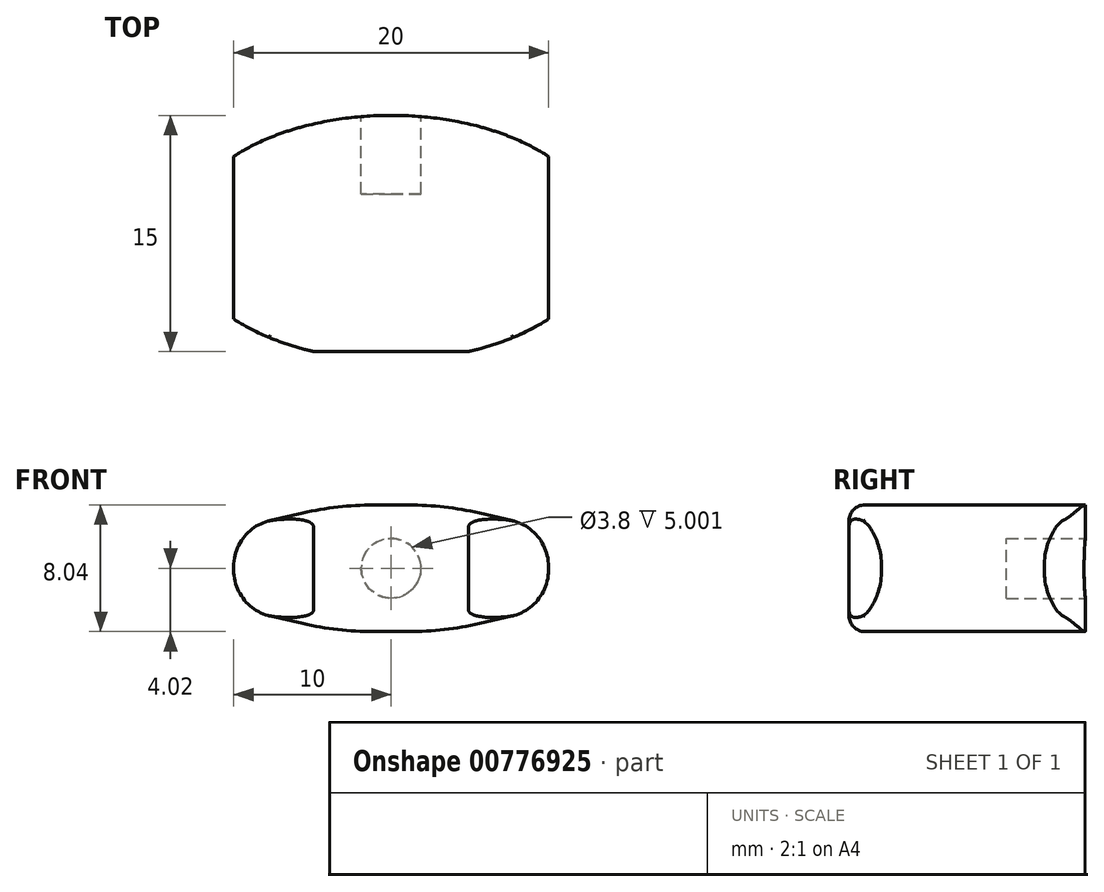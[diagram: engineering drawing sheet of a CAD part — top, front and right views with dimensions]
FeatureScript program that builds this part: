
annotation { "Feature Type Name" : "Feature", "Feature Type Description" : "" }
export const myFeature = defineFeature(function(context is Context, id is Id, definition is map)
    precondition{}
    {
        {
            var Q0;
            Q0=qCreatedBy(makeId("Front.planeOp"),FACE);
            var sketch = newSketch(context, id + "F0", { "sketchPlane" : qUnion([Q0])});
            skLineSegment(sketch, "E0.bottom", {"start": v(3.4, -4.02) * mm, "end": v(-3.4, -4.02) * mm});
            skLineSegment(sketch, "E0.top", {"start": v(3.4, 4.02) * mm, "end": v(-3.4, 4.02) * mm});
            skLineSegment(sketch, "E0.left", {"start": v(10, -2.5) * mm, "end": v(10, 2.5) * mm});
            skLineSegment(sketch, "E0.right", {"start": v(-10, -2.5) * mm, "end": v(-10, 2.5) * mm});
            skPoint(sketch, "E0.middle", {"position": v(0, 0) * mm});
            skLineSegment(sketch, "E1", {"start": v(10, -2.5) * mm, "end": v(3.4, -4.02) * mm});
            skPoint(sketch, "E2.orphan", {"position": v(10, -4.02) * mm});
            skLineSegment(sketch, "E3.MirrorCS", {"start": v(10, 2.5) * mm, "end": v(3.4, 4.02) * mm});
            skLineSegment(sketch, "E4.MirrorCS", {"start": v(-10, -2.5) * mm, "end": v(-3.4, -4.02) * mm});
            skLineSegment(sketch, "E5.MirrorCS", {"start": v(-10, 2.5) * mm, "end": v(-3.4, 4.02) * mm});
            skPoint(sketch, "E6.orphan", {"position": v(10, 4.02) * mm});
            skPoint(sketch, "E7.orphan", {"position": v(-10, 4.02) * mm});
            skPoint(sketch, "E8.orphan", {"position": v(-10, -4.02) * mm});
            skSolve(sketch);
        }
        {
            var Q0;
            Q0 = qSketchRegion(id + "F0", true);
            extrude(context, id + "F1", {"entities" : qUnion([Q0]), "depth" : 15 * mm, "offsetDistance" : 25 * mm});
        }
        {
            var Q0;
            Q0=qCreatedBy(makeId("Front.planeOp"),FACE);
            var sketch = newSketch(context, id + "F2", { "sketchPlane" : qUnion([Q0])});
            skCircle(sketch, "E9", {"center": v(0, 0) * mm, "radius": 1.9 * mm});
            skSolve(sketch);
        }
        {
            var Q0;
            Q0 = qSketchRegion(id + "F2", true);
            extrude(context, id + "F3", {"entities" : qUnion([Q0]), "operationType" : NewBodyOperationType.REMOVE, "depth" : 5 * mm, "offsetDistance" : 25 * mm});
        }
        {
            var Q0;
            Q0=qCreatedBy(makeId("Top.planeOp"),FACE);
            var sketch = newSketch(context, id + "F4", { "sketchPlane" : qUnion([Q0])});
            skEllipse(sketch, "E10", {"center": v(0, -7.77) * mm, "majorRadius": 7.77 * mm, "minorRadius": 13.38 * mm, "majorAxis": v(0, 1)});
            skSolve(sketch);
        }
        {
            var Q0;
            Q0 = qSketchRegion(id + "F4", true);
            extrude(context, id + "F5", {"entities" : qUnion([Q0]), "operationType" : NewBodyOperationType.INTERSECT, "oppositeDirection" : true, "depth" : 25 * mm, "offsetDistance" : 25 * mm, "hasSecondDirection" : true, "secondDirectionOppositeDirection" : false, "secondDirectionDepth" : 25 * mm});
        }
        {
            var Q0;
            Q0=makeQuery(id+"F1.opExtrude","SWEPT_EDGE",EDGE,{"disambiguationData":[OSD([sQuery(id+"F0.wireOp",EDGE,"E0.bottom"),sQuery(id+"F0.wireOp",EDGE,"E1")])]});
            var Q1;
            Q1=makeQuery(id+"F1.opExtrude","SWEPT_EDGE",EDGE,{"disambiguationData":[OSD([sQuery(id+"F0.wireOp",EDGE,"E0.bottom"),sQuery(id+"F0.wireOp",EDGE,"E4.MirrorCS")])]});
            var Q2;
            Q2=makeQuery(id+"F1.opExtrude","SWEPT_EDGE",EDGE,{"disambiguationData":[OSD([sQuery(id+"F0.wireOp",EDGE,"E0.top"),sQuery(id+"F0.wireOp",EDGE,"E3.MirrorCS")])]});
            var Q3;
            Q3=makeQuery(id+"F1.opExtrude","SWEPT_EDGE",EDGE,{"disambiguationData":[OSD([sQuery(id+"F0.wireOp",EDGE,"E0.top"),sQuery(id+"F0.wireOp",EDGE,"E5.MirrorCS")])]});
            fillet(context, id + "F6", {"entities" : qUnion([Q0, Q1, Q2, Q3]), "radius" : 20 * mm, "tangentPropagation" : true, "allowEdgeOverflow" : false});
        }
        {
            var Q0;
            Q0=makeQuery(id+"F1.opExtrude","SWEPT_EDGE",EDGE,{"disambiguationData":[OSD([sQuery(id+"F0.wireOp",EDGE,"E0.right"),sQuery(id+"F0.wireOp",EDGE,"E4.MirrorCS")])]});
            var Q1;
            Q1=makeQuery(id+"F1.opExtrude","SWEPT_EDGE",EDGE,{"disambiguationData":[OSD([sQuery(id+"F0.wireOp",EDGE,"E0.right"),sQuery(id+"F0.wireOp",EDGE,"E5.MirrorCS")])]});
            var Q2;
            Q2=makeQuery(id+"F1.opExtrude","SWEPT_EDGE",EDGE,{"disambiguationData":[OSD([sQuery(id+"F0.wireOp",EDGE,"E0.left"),sQuery(id+"F0.wireOp",EDGE,"E1")])]});
            var Q3;
            Q3=makeQuery(id+"F1.opExtrude","SWEPT_EDGE",EDGE,{"disambiguationData":[OSD([sQuery(id+"F0.wireOp",EDGE,"E0.left"),sQuery(id+"F0.wireOp",EDGE,"E3.MirrorCS")])]});
            fillet(context, id + "F7", {"entities" : qUnion([Q0, Q1, Q2, Q3]), "radius" : 3 * mm, "tangentPropagation" : true, "allowEdgeOverflow" : false});
        }
        {
            var Q0;
            {var subQ0=sQuery(id+"F0.wireOp",EDGE,"E0.top");var subQ1=sQuery(id+"F0.wireOp",EDGE,"E3.MirrorCS");Q0=makeQuery(id+"F6.opFillet","BLEND_EDGE",EDGE,{"blendedFrom":[makeQuery(id+"F1.opExtrude","SWEPT_EDGE",EDGE,{"disambiguationData":[OSD([subQ0,subQ1])]}),makeQuery(id+"F5.boolean.opBoolean","COPY",FACE,{"disambiguationData":[TD([makeQuery(id+"F1.opExtrude","SWEPT_FACE",FACE,{"disambiguationData":[OSD([sQuery(id+"F0.wireOp",EDGE,"E0.bottom")])]}),makeQuery(id+"F1.opExtrude","SWEPT_FACE",FACE,{"disambiguationData":[OSD([subQ0])]}),makeQuery(id+"F1.opExtrude","SWEPT_FACE",FACE,{"disambiguationData":[OSD([sQuery(id+"F0.wireOp",EDGE,"E0.left")])]}),makeQuery(id+"F1.opExtrude","SWEPT_FACE",FACE,{"disambiguationData":[OSD([sQuery(id+"F0.wireOp",EDGE,"E0.right")])]}),makeQuery(id+"F1.opExtrude","SWEPT_FACE",FACE,{"disambiguationData":[OSD([sQuery(id+"F0.wireOp",EDGE,"E1")])]}),makeQuery(id+"F1.opExtrude","SWEPT_FACE",FACE,{"disambiguationData":[OSD([subQ1])]}),makeQuery(id+"F1.opExtrude","SWEPT_FACE",FACE,{"disambiguationData":[OSD([sQuery(id+"F0.wireOp",EDGE,"E4.MirrorCS")])]}),makeQuery(id+"F1.opExtrude","SWEPT_FACE",FACE,{"disambiguationData":[OSD([sQuery(id+"F0.wireOp",EDGE,"E5.MirrorCS")])]}),makeQuery(id+"F3.boolean.opBoolean","COPY",FACE,{"derivedFrom":makeQuery(id+"F3.opExtrude","SWEPT_FACE",FACE,{"disambiguationData":[OSD([sQuery(id+"F2.wireOp",EDGE,"E9")])]})})])],"derivedFrom":makeQuery(id+"F5.boolean.toolComplement.opBoolean","COPY",FACE,{"derivedFrom":makeQuery(id+"F5.opExtrude","SWEPT_FACE",FACE,{"disambiguationData":[OSD([sQuery(id+"F4.wireOp",EDGE,"E10")])]})})})],"blendedInto":[makeQuery(id+"F5.boolean.opBoolean","COPY",FACE,{"disambiguationData":[TD([makeQuery(id+"F1.opExtrude","SWEPT_FACE",FACE,{"disambiguationData":[OSD([sQuery(id+"F0.wireOp",EDGE,"E0.bottom")])]}),makeQuery(id+"F1.opExtrude","SWEPT_FACE",FACE,{"disambiguationData":[OSD([subQ0])]}),makeQuery(id+"F1.opExtrude","SWEPT_FACE",FACE,{"disambiguationData":[OSD([sQuery(id+"F0.wireOp",EDGE,"E0.left")])]}),makeQuery(id+"F1.opExtrude","SWEPT_FACE",FACE,{"disambiguationData":[OSD([sQuery(id+"F0.wireOp",EDGE,"E0.right")])]}),makeQuery(id+"F1.opExtrude","SWEPT_FACE",FACE,{"disambiguationData":[OSD([sQuery(id+"F0.wireOp",EDGE,"E1")])]}),makeQuery(id+"F1.opExtrude","SWEPT_FACE",FACE,{"disambiguationData":[OSD([subQ1])]}),makeQuery(id+"F1.opExtrude","SWEPT_FACE",FACE,{"disambiguationData":[OSD([sQuery(id+"F0.wireOp",EDGE,"E4.MirrorCS")])]}),makeQuery(id+"F1.opExtrude","SWEPT_FACE",FACE,{"disambiguationData":[OSD([sQuery(id+"F0.wireOp",EDGE,"E5.MirrorCS")])]}),makeQuery(id+"F3.boolean.opBoolean","COPY",FACE,{"derivedFrom":makeQuery(id+"F3.opExtrude","SWEPT_FACE",FACE,{"disambiguationData":[OSD([sQuery(id+"F2.wireOp",EDGE,"E9")])]})})])],"derivedFrom":makeQuery(id+"F5.boolean.toolComplement.opBoolean","COPY",FACE,{"derivedFrom":makeQuery(id+"F5.opExtrude","SWEPT_FACE",FACE,{"disambiguationData":[OSD([sQuery(id+"F4.wireOp",EDGE,"E10")])]})})})]});}
            var Q1;
            {var subQ0=sQuery(id+"F0.wireOp",EDGE,"E3.MirrorCS");var subQ1=sQuery(id+"F0.wireOp",EDGE,"E1");var subQ2=sQuery(id+"F0.wireOp",EDGE,"E0.left");Q1=makeQuery(id+"F7.opFillet","BLEND_EDGE",EDGE,{"blendedFrom":[makeQuery(id+"F1.opExtrude","SWEPT_EDGE",EDGE,{"disambiguationData":[OSD([subQ2,subQ0])]}),makeQuery(id+"F5.boolean.opBoolean","COPY",FACE,{"disambiguationData":[TD([makeQuery(id+"F1.opExtrude","CAP_FACE",FACE,{"disambiguationData":[OSD([sQuery(id+"F0.wireOp",EDGE,"E0.bottom"),sQuery(id+"F0.wireOp",EDGE,"E0.top"),subQ2,sQuery(id+"F0.wireOp",EDGE,"E0.right"),subQ1,subQ0,sQuery(id+"F0.wireOp",EDGE,"E4.MirrorCS"),sQuery(id+"F0.wireOp",EDGE,"E5.MirrorCS")])],"isStart":false}),makeQuery(id+"F1.opExtrude","SWEPT_FACE",FACE,{"disambiguationData":[OSD([subQ2])]}),makeQuery(id+"F1.opExtrude","SWEPT_FACE",FACE,{"disambiguationData":[OSD([subQ1])]}),makeQuery(id+"F1.opExtrude","SWEPT_FACE",FACE,{"disambiguationData":[OSD([subQ0])]})])],"derivedFrom":makeQuery(id+"F5.boolean.toolComplement.opBoolean","COPY",FACE,{"derivedFrom":makeQuery(id+"F5.opExtrude","SWEPT_FACE",FACE,{"disambiguationData":[OSD([sQuery(id+"F4.wireOp",EDGE,"E10")])]})})})],"blendedInto":[makeQuery(id+"F5.boolean.opBoolean","COPY",FACE,{"disambiguationData":[TD([makeQuery(id+"F1.opExtrude","CAP_FACE",FACE,{"disambiguationData":[OSD([sQuery(id+"F0.wireOp",EDGE,"E0.bottom"),sQuery(id+"F0.wireOp",EDGE,"E0.top"),subQ2,sQuery(id+"F0.wireOp",EDGE,"E0.right"),subQ1,subQ0,sQuery(id+"F0.wireOp",EDGE,"E4.MirrorCS"),sQuery(id+"F0.wireOp",EDGE,"E5.MirrorCS")])],"isStart":false}),makeQuery(id+"F1.opExtrude","SWEPT_FACE",FACE,{"disambiguationData":[OSD([subQ2])]}),makeQuery(id+"F1.opExtrude","SWEPT_FACE",FACE,{"disambiguationData":[OSD([subQ1])]}),makeQuery(id+"F1.opExtrude","SWEPT_FACE",FACE,{"disambiguationData":[OSD([subQ0])]})])],"derivedFrom":makeQuery(id+"F5.boolean.toolComplement.opBoolean","COPY",FACE,{"derivedFrom":makeQuery(id+"F5.opExtrude","SWEPT_FACE",FACE,{"disambiguationData":[OSD([sQuery(id+"F4.wireOp",EDGE,"E10")])]})})})]});}
            var Q2;
            {var subQ0=sQuery(id+"F0.wireOp",EDGE,"E5.MirrorCS");var subQ1=sQuery(id+"F0.wireOp",EDGE,"E0.top");Q2=makeQuery(id+"F6.opFillet","BLEND_EDGE",EDGE,{"blendedFrom":[makeQuery(id+"F1.opExtrude","SWEPT_EDGE",EDGE,{"disambiguationData":[OSD([subQ1,subQ0])]}),makeQuery(id+"F1.opExtrude","CAP_FACE",FACE,{"disambiguationData":[OSD([sQuery(id+"F0.wireOp",EDGE,"E0.bottom"),subQ1,sQuery(id+"F0.wireOp",EDGE,"E0.left"),sQuery(id+"F0.wireOp",EDGE,"E0.right"),sQuery(id+"F0.wireOp",EDGE,"E1"),sQuery(id+"F0.wireOp",EDGE,"E3.MirrorCS"),sQuery(id+"F0.wireOp",EDGE,"E4.MirrorCS"),subQ0])],"isStart":false})],"blendedInto":[makeQuery(id+"F1.opExtrude","CAP_FACE",FACE,{"disambiguationData":[OSD([sQuery(id+"F0.wireOp",EDGE,"E0.bottom"),subQ1,sQuery(id+"F0.wireOp",EDGE,"E0.left"),sQuery(id+"F0.wireOp",EDGE,"E0.right"),sQuery(id+"F0.wireOp",EDGE,"E1"),sQuery(id+"F0.wireOp",EDGE,"E3.MirrorCS"),sQuery(id+"F0.wireOp",EDGE,"E4.MirrorCS"),subQ0])],"isStart":false})]});}
            var Q3;
            {var subQ0=sQuery(id+"F0.wireOp",EDGE,"E4.MirrorCS");var subQ1=sQuery(id+"F0.wireOp",EDGE,"E0.bottom");Q3=makeQuery(id+"F6.opFillet","BLEND_EDGE",EDGE,{"blendedFrom":[makeQuery(id+"F1.opExtrude","SWEPT_EDGE",EDGE,{"disambiguationData":[OSD([subQ1,subQ0])]}),makeQuery(id+"F1.opExtrude","CAP_FACE",FACE,{"disambiguationData":[OSD([subQ1,sQuery(id+"F0.wireOp",EDGE,"E0.top"),sQuery(id+"F0.wireOp",EDGE,"E0.left"),sQuery(id+"F0.wireOp",EDGE,"E0.right"),sQuery(id+"F0.wireOp",EDGE,"E1"),sQuery(id+"F0.wireOp",EDGE,"E3.MirrorCS"),subQ0,sQuery(id+"F0.wireOp",EDGE,"E5.MirrorCS")])],"isStart":false})],"blendedInto":[makeQuery(id+"F1.opExtrude","CAP_FACE",FACE,{"disambiguationData":[OSD([subQ1,sQuery(id+"F0.wireOp",EDGE,"E0.top"),sQuery(id+"F0.wireOp",EDGE,"E0.left"),sQuery(id+"F0.wireOp",EDGE,"E0.right"),sQuery(id+"F0.wireOp",EDGE,"E1"),sQuery(id+"F0.wireOp",EDGE,"E3.MirrorCS"),subQ0,sQuery(id+"F0.wireOp",EDGE,"E5.MirrorCS")])],"isStart":false})]});}
            var Q4;
            {var subQ0=sQuery(id+"F0.wireOp",EDGE,"E5.MirrorCS");var subQ1=sQuery(id+"F0.wireOp",EDGE,"E4.MirrorCS");var subQ2=sQuery(id+"F0.wireOp",EDGE,"E0.right");Q4=makeQuery(id+"F7.opFillet","BLEND_EDGE",EDGE,{"blendedFrom":[makeQuery(id+"F1.opExtrude","SWEPT_EDGE",EDGE,{"disambiguationData":[OSD([subQ2,subQ1])]}),makeQuery(id+"F5.boolean.opBoolean","COPY",FACE,{"disambiguationData":[TD([makeQuery(id+"F1.opExtrude","CAP_FACE",FACE,{"disambiguationData":[OSD([sQuery(id+"F0.wireOp",EDGE,"E0.bottom"),sQuery(id+"F0.wireOp",EDGE,"E0.top"),sQuery(id+"F0.wireOp",EDGE,"E0.left"),subQ2,sQuery(id+"F0.wireOp",EDGE,"E1"),sQuery(id+"F0.wireOp",EDGE,"E3.MirrorCS"),subQ1,subQ0])],"isStart":false}),makeQuery(id+"F1.opExtrude","SWEPT_FACE",FACE,{"disambiguationData":[OSD([subQ2])]}),makeQuery(id+"F1.opExtrude","SWEPT_FACE",FACE,{"disambiguationData":[OSD([subQ1])]}),makeQuery(id+"F1.opExtrude","SWEPT_FACE",FACE,{"disambiguationData":[OSD([subQ0])]})])],"derivedFrom":makeQuery(id+"F5.boolean.toolComplement.opBoolean","COPY",FACE,{"derivedFrom":makeQuery(id+"F5.opExtrude","SWEPT_FACE",FACE,{"disambiguationData":[OSD([sQuery(id+"F4.wireOp",EDGE,"E10")])]})})})],"blendedInto":[makeQuery(id+"F5.boolean.opBoolean","COPY",FACE,{"disambiguationData":[TD([makeQuery(id+"F1.opExtrude","CAP_FACE",FACE,{"disambiguationData":[OSD([sQuery(id+"F0.wireOp",EDGE,"E0.bottom"),sQuery(id+"F0.wireOp",EDGE,"E0.top"),sQuery(id+"F0.wireOp",EDGE,"E0.left"),subQ2,sQuery(id+"F0.wireOp",EDGE,"E1"),sQuery(id+"F0.wireOp",EDGE,"E3.MirrorCS"),subQ1,subQ0])],"isStart":false}),makeQuery(id+"F1.opExtrude","SWEPT_FACE",FACE,{"disambiguationData":[OSD([subQ2])]}),makeQuery(id+"F1.opExtrude","SWEPT_FACE",FACE,{"disambiguationData":[OSD([subQ1])]}),makeQuery(id+"F1.opExtrude","SWEPT_FACE",FACE,{"disambiguationData":[OSD([subQ0])]})])],"derivedFrom":makeQuery(id+"F5.boolean.toolComplement.opBoolean","COPY",FACE,{"derivedFrom":makeQuery(id+"F5.opExtrude","SWEPT_FACE",FACE,{"disambiguationData":[OSD([sQuery(id+"F4.wireOp",EDGE,"E10")])]})})})]});}
            fillet(context, id + "F8", {"entities" : qUnion([Q0, Q1, Q2, Q3, Q4]), "radius" : 1 * mm, "tangentPropagation" : true, "allowEdgeOverflow" : false});
        }
    });
